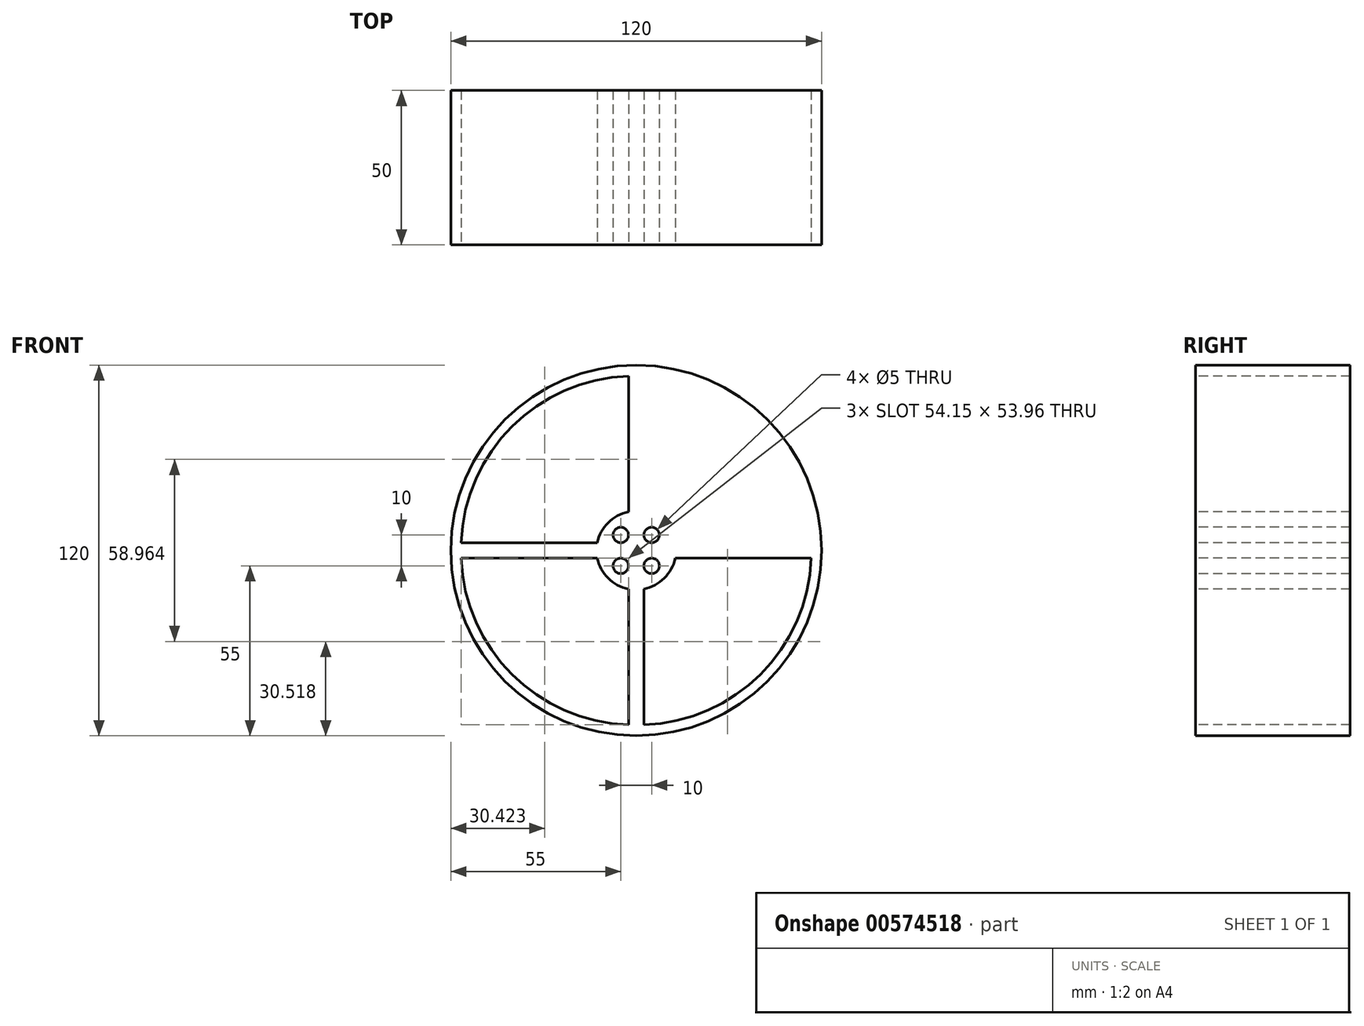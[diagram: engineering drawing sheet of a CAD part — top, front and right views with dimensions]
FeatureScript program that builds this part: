
annotation { "Feature Type Name" : "Feature", "Feature Type Description" : "" }
export const myFeature = defineFeature(function(context is Context, id is Id, definition is map)
    precondition{}
    {
        {
            var Q0;
            Q0=qCreatedBy(makeId("Front.planeOp"),FACE);
            var sketch = newSketch(context, id + "F0", { "sketchPlane" : qUnion([Q0])});
            skCircle(sketch, "E0", {"center": v(0, 0) * mm, "radius": 60 * mm});
            skSolve(sketch);
        }
        {
            var Q0;
            Q0=makeQuery(id+"F0.imprint","IMPRINT",FACE,{"disambiguationData":[TD([[makeQuery(id+"F0.imprint","IMPRINT",EDGE,{"derivedFrom":sQuery(id+"F0.wireOp",EDGE,"E0")}),1.0]])]});
            extrude(context, id + "F1", {"entities" : qUnion([Q0]), "endBound" : BoundingType.SYMMETRIC, "depth" : 50 * mm, "offsetDistance" : 25 * mm});
        }
        {
            var Q0;
            Q0=makeQuery(id+"F1.opExtrude","CAP_FACE",FACE,{"disambiguationData":[OSD([sQuery(id+"F0.wireOp",EDGE,"E0")])],"isStart":false});
            cPlane(context, id + "F2", {"entities" : qUnion([Q0]), "cplaneType" : CPlaneType.OFFSET, "offset" : 0 * mm, "width" : 150 * mm, "height" : 150 * mm});
        }
        {
            var Q0;
            Q0=qCreatedBy(id+"F2.planeOp",FACE);
            var sketch = newSketch(context, id + "F3", { "sketchPlane" : qUnion([Q0])});
            skCircle(sketch, "E1", {"center": v(0, 0) * mm, "radius": 10 * mm});
            skLineSegment(sketch, "E2", {"start": v(0, 59.77) * mm, "end": v(0, -59.77) * mm, "construction": true});
            skLineSegment(sketch, "E3", {"start": v(-60.05, 0) * mm, "end": v(59.77, 0) * mm, "construction": true});
            skLineSegment(sketch, "E4", {"start": v(-2.5, 12.46) * mm, "end": v(-2.5, 56.46) * mm});
            skLineSegment(sketch, "E5", {"start": v(-56.65, 2.5) * mm, "end": v(-12.65, 2.5) * mm});
            skArc(sketch, "E6", {"start": v(-2.5, 56.46) * mm, "mid": v(-40.2, 40.14) * mm, "end": v(-56.65, 2.5) * mm});
            skArc(sketch, "E7", {"start": v(-2.5, 12.46) * mm, "mid": v(-9.06, 9) * mm, "end": v(-12.65, 2.5) * mm});
            skArc(sketch, "E8.MirrorCS", {"start": v(2.5, 56.46) * mm, "mid": v(40.2, 40.14) * mm, "end": v(56.65, 2.5) * mm});
            skLineSegment(sketch, "E9.MirrorCS", {"start": v(2.5, 12.46) * mm, "end": v(2.5, 56.46) * mm});
            skArc(sketch, "E10.MirrorCS", {"start": v(2.5, 12.46) * mm, "mid": v(9.06, 9) * mm, "end": v(12.65, 2.5) * mm});
            skLineSegment(sketch, "E11.MirrorCS", {"start": v(56.65, 2.5) * mm, "end": v(12.65, 2.5) * mm});
            skLineSegment(sketch, "E12.MirrorCS", {"start": v(-56.65, -2.5) * mm, "end": v(-12.65, -2.5) * mm});
            skArc(sketch, "E13.MirrorCS", {"start": v(-2.5, -12.46) * mm, "mid": v(-9.06, -9) * mm, "end": v(-12.65, -2.5) * mm});
            skLineSegment(sketch, "E14.MirrorCS", {"start": v(-2.5, -12.46) * mm, "end": v(-2.5, -56.46) * mm});
            skArc(sketch, "E15.MirrorCS", {"start": v(-2.5, -56.46) * mm, "mid": v(-40.2, -40.14) * mm, "end": v(-56.65, -2.5) * mm});
            skLineSegment(sketch, "E16.MirrorCS", {"start": v(2.5, -12.46) * mm, "end": v(2.5, -56.46) * mm});
            skArc(sketch, "E17.MirrorCS", {"start": v(2.5, -56.46) * mm, "mid": v(40.2, -40.14) * mm, "end": v(56.65, -2.5) * mm});
            skLineSegment(sketch, "E18.MirrorCS", {"start": v(56.65, -2.5) * mm, "end": v(12.65, -2.5) * mm});
            skArc(sketch, "E19.MirrorCS", {"start": v(2.5, -12.46) * mm, "mid": v(9.06, -9) * mm, "end": v(12.65, -2.5) * mm});
            skPoint(sketch, "E20", {"position": v(-5, 5) * mm});
            skPoint(sketch, "E21.MirrorP", {"position": v(5, 5) * mm});
            skPoint(sketch, "E22.MirrorP", {"position": v(-5, -5) * mm});
            skPoint(sketch, "E23.MirrorP", {"position": v(5, -5) * mm});
            skSolve(sketch);
        }
        {
            var Q0;
            Q0=makeQuery(id+"F3.imprint","IMPRINT",FACE,{"disambiguationData":[TD([[makeQuery(id+"F3.imprint","IMPRINT",EDGE,{"derivedFrom":sQuery(id+"F3.wireOp",EDGE,"E4")}),1.0]])]});
            extrude(context, id + "F4", {"entities" : qUnion([Q0]), "operationType" : NewBodyOperationType.REMOVE, "endBound" : BoundingType.SYMMETRIC, "oppositeDirection" : true, "depth" : 101.2 * mm, "offsetDistance" : 25 * mm});
        }
        {
            var Q0;
            Q0=makeQuery(id+"F3.imprint","IMPRINT",FACE,{"disambiguationData":[TD([[makeQuery(id+"F3.imprint","IMPRINT",EDGE,{"derivedFrom":sQuery(id+"F3.wireOp",EDGE,"E12.MirrorCS")}),-1.0]])]});
            var Q1;
            Q1=makeQuery(id+"F3.imprint","IMPRINT",FACE,{"disambiguationData":[TD([[makeQuery(id+"F3.imprint","IMPRINT",EDGE,{"derivedFrom":sQuery(id+"F3.wireOp",EDGE,"E16.MirrorCS")}),1.0]])]});
            var Q2;
            Q2=makeQuery(id+"F3.imprint","IMPRINT",FACE,{"disambiguationData":[TD([[makeQuery(id+"F3.imprint","IMPRINT",EDGE,{"derivedFrom":sQuery(id+"F3.wireOp",EDGE,"E8.MirrorCS")}),-1.0]])]});
            extrude(context, id + "F5", {"entities" : qUnion([Q0, Q1, Q2]), "operationType" : NewBodyOperationType.REMOVE, "endBound" : BoundingType.SYMMETRIC, "oppositeDirection" : true, "depth" : 100 * mm, "offsetDistance" : 25 * mm});
        }
        {
            var Q0;
            Q0=sQuery(id+"F3.wireOp",VERTEX,"E22.MirrorP");
            var Q1;
            Q1=sQuery(id+"F3.wireOp",VERTEX,"E20");
            var Q2;
            Q2=sQuery(id+"F3.wireOp",VERTEX,"E21.MirrorP");
            var Q3;
            Q3=sQuery(id+"F3.wireOp",VERTEX,"E23.MirrorP");
            var Q4;
            Q4=makeQuery(id+"F1.opExtrude","SWEPT_BODY",BODY,{"disambiguationData":[OSD([sQuery(id+"F0.wireOp",EDGE,"E0")])]});
            hole(context, id + "F6", {"style" : HoleStyle.SIMPLE, "endStyle" : HoleEndStyle.THROUGH, "holeDiameter" : 5 * mm, "isTappedThrough" : true, "tappedDepth" : 12 * mm, "tapClearance" : 3, "locations" : qUnion([Q0, Q1, Q2, Q3]), "scope" : qUnion([Q4])});
        }
    });
